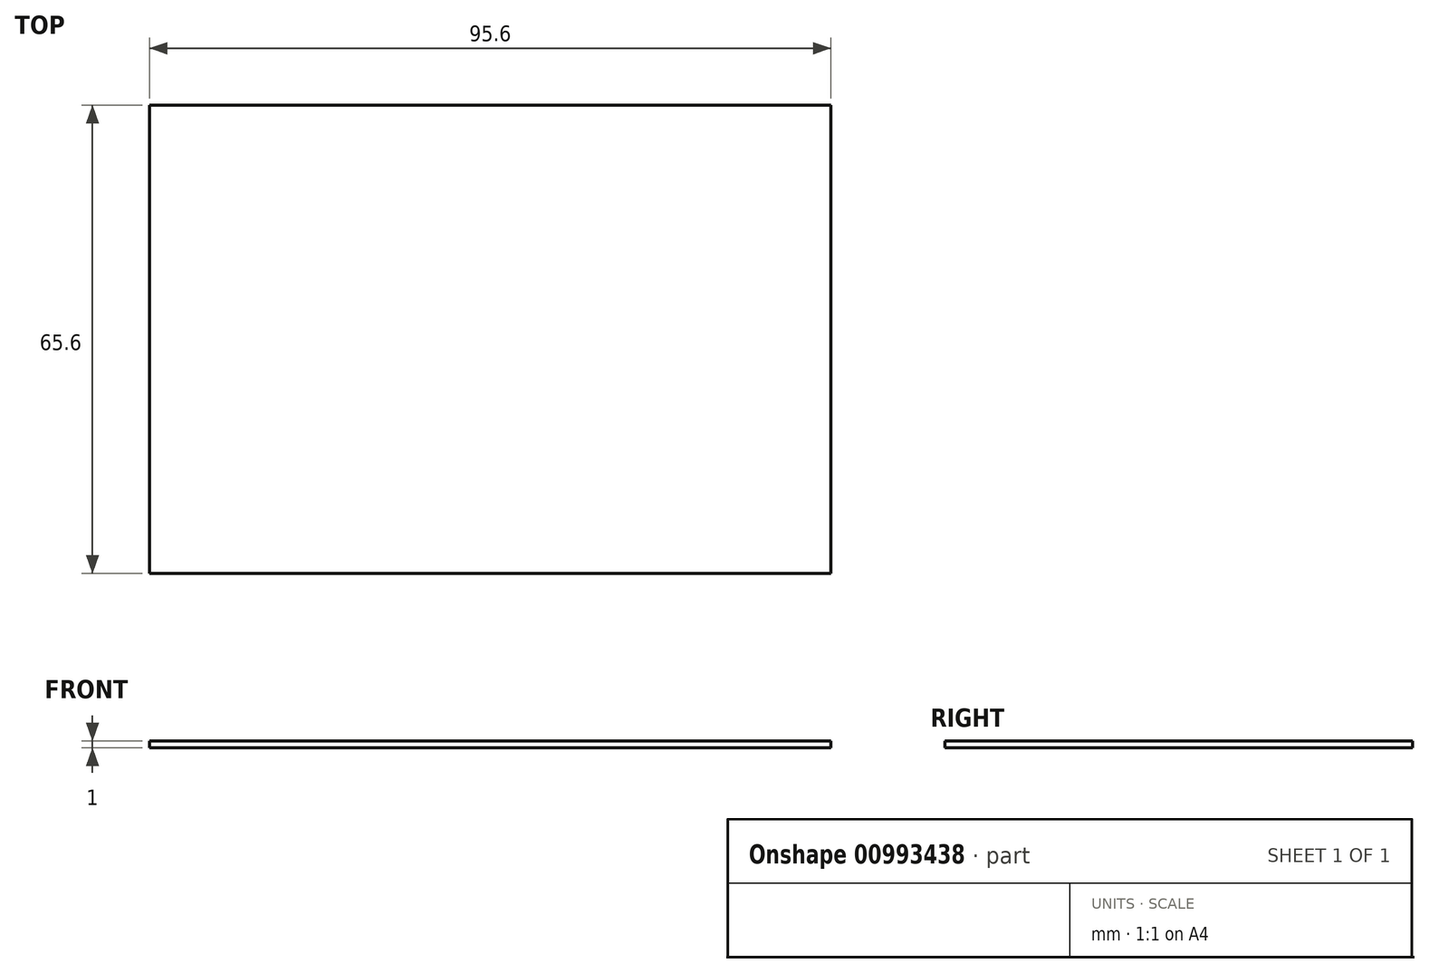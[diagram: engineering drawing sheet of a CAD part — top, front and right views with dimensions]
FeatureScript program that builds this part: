
annotation { "Feature Type Name" : "Feature", "Feature Type Description" : "" }
export const myFeature = defineFeature(function(context is Context, id is Id, definition is map)
    precondition{}
    {
        {
            var Q0;
            Q0=qCreatedBy(makeId("Top.planeOp"),FACE);
            var sketch = newSketch(context, id + "F0", { "sketchPlane" : qUnion([Q0])});
            skLineSegment(sketch, "E0.bottom", {"start": v(47.8, -32.8) * mm, "end": v(-47.8, -32.8) * mm});
            skLineSegment(sketch, "E0.top", {"start": v(47.8, 32.8) * mm, "end": v(-47.8, 32.8) * mm});
            skLineSegment(sketch, "E0.left", {"start": v(47.8, -32.8) * mm, "end": v(47.8, 32.8) * mm});
            skLineSegment(sketch, "E0.right", {"start": v(-47.8, -32.8) * mm, "end": v(-47.8, 32.8) * mm});
            skPoint(sketch, "E0.middle", {"position": v(0, 0) * mm});
            skSolve(sketch);
        }
        {
            var Q0;
            Q0=makeQuery(id+"F0.imprint","IMPRINT",FACE,{"disambiguationData":[TD([[makeQuery(id+"F0.imprint","IMPRINT",EDGE,{"derivedFrom":sQuery(id+"F0.wireOp",EDGE,"E0.bottom")}),-1.0]])]});
            extrude(context, id + "F1", {"entities" : qUnion([Q0]), "depth" : 1 * mm, "offsetDistance" : 25 * mm});
        }
    });
